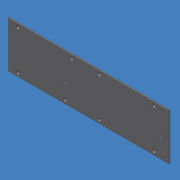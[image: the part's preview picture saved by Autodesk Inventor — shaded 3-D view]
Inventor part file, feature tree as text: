
AUTODESK INVENTOR PART (.ipt)
format: ipt  version: unknown  size: 222,208 bytes
history: native  units: mm (DEFAULTED — no unit token found)
features: sketch x4, extrude x2, hole x2
ambient origin geometry x8: Origin, YZ Plane, XZ Plane, XY Plane, X Axis, Y Axis, Z Axis, Center Point
feature tree (8):
  extrude  "Extrusion1"  Depth=79.4258mm
  extrude  "Extrusion2"  Depth=16.3068mm
  hole  "Hole1"  [1 undecoded]
  hole  "Hole2"  [1 undecoded]
  sketch  "Sketch1"  dims[d0=277.622mm d1=79.4258mm]
  sketch  "Sketch2"  dims[d2=2.2098mm d3=0.0mm d4=16.3068mm]
  sketch  "Sketch3"  dims[d5=5.7912mm d6=5.7912mm]
  sketch  "Sketch4"  dims[d7=26.2382mm d8=120.7262mm d9=168.3004mm d10=179.7812mm d11=6.6802mm d12=4.5974mm d13=0.0mm d14=3.1496mm d15=12.7mm d16=6.731mm d17=6.35mm d18=14.3117mm d19=19.05mm d20=20.594885mm d21=47.371mm d22=14.6812mm d23=165.1mm d24=5.2324mm d25=12.7mm d26=6.731mm d27=6.35mm d28=14.3117mm d29=19.05mm d30=20.594885mm]
note: 2 required parameter values undecoded (feature->parameter linkage not recoverable at this tier; creation-order binding heuristic only, values carry confidence <= 0.55)
